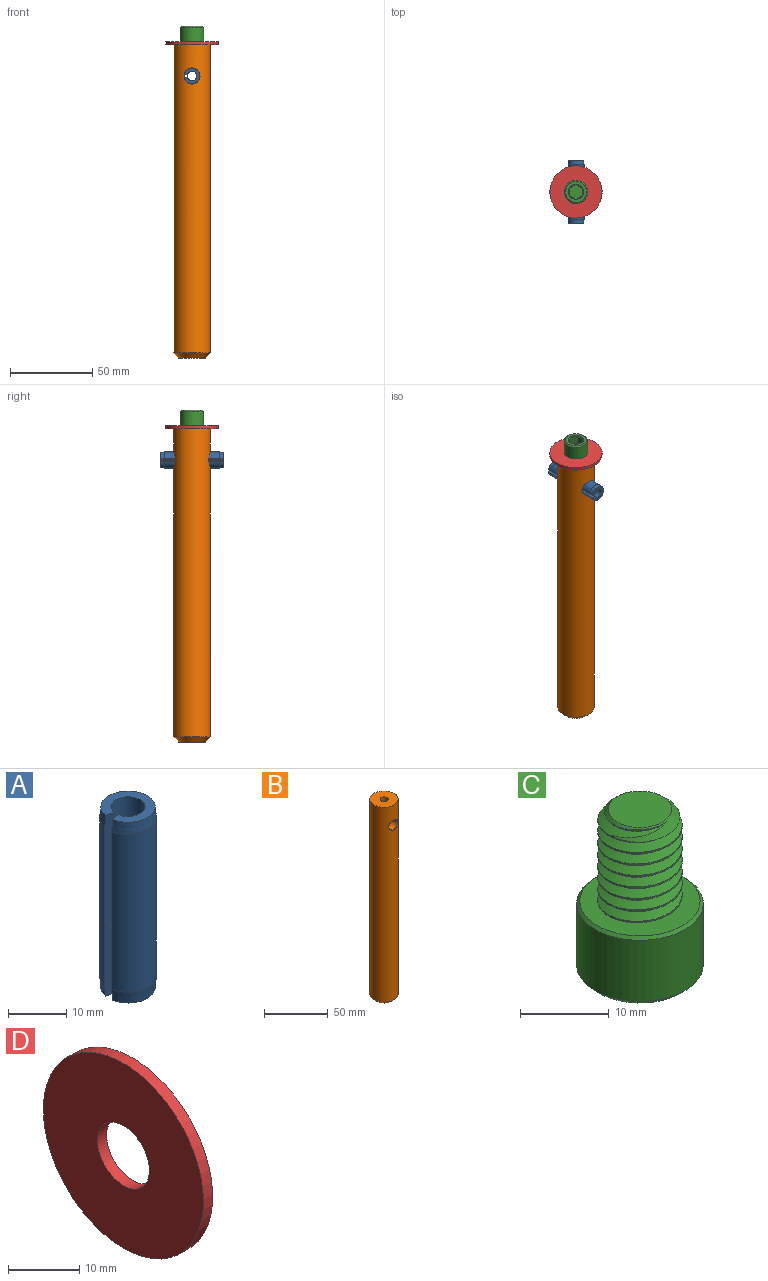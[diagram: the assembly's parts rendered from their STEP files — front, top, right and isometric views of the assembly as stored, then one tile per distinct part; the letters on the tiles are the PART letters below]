
ASSEMBLY  parts=4 mates=3
PART A: 8 faces, bbox 9.7x9.8x38.1 mm
  f0: cylinder r=2.93mm len=38.1mm, axis (0,0,-1), area 663.3mm2, adj f1,f3,f4,f5
  f1: plane 38.1x1.93mm, normal (-0.17,0.98,0), area 74mm2, adj f0,f2,f4,f5,f6,f7
  f2: cylinder r=4.89mm len=33.27mm, axis (0,0,-1), area 965.4mm2, adj f1,f3,f6,f7
  f3: plane 38.1x1.93mm, normal (-0.17,-0.98,0), area 74mm2, adj f0,f2,f4,f5,f6,f7
  f4: plane 9.35x9.28mm, normal (0,0,1), area 39.3mm2, adj f0,f1,f3,f7
  f5: plane 9.35x9.28mm, normal (0,0,-1), area 39.3mm2, adj f0,f1,f3,f6
  f6: cone r=4.89mm half-angle=5.1deg, axis (0,0,1), area 68.7mm2, adj f1,f2,f3,f5
  f7: cone r=4.67mm half-angle=5.1deg, axis (0,0,-1), area 68.7mm2, adj f1,f2,f3,f4
PART B: 7 faces, bbox 22.2x22.2x190.5 mm
  f0: cylinder r=11.11mm len=187.33mm, axis (0,0,-1), area 12933.5mm2, adj f1,f3,f4
  f1: plane 22.23x22.23mm, normal (0,0,1), area 356.3mm2, adj f0,f5
  f2: plane 15.88x15.88mm, normal (0,0,-1), area 197.9mm2, adj f3
  f3: cone r=11.11mm half-angle=45deg, axis (0,0,1), area 268.7mm2, adj f0,f2
  f4: cylinder r=4.76mm len=22.23mm, axis (0,-1,0), area 633.4mm2, adj f0
  f5: cylinder r=3.17mm len=12.7mm, axis (0,0,1), area 253.4mm2, adj f1,f6
  f6: plane 6.35x6.35mm, normal (0,0,1), area 31.7mm2, adj f5
PART C: 24 faces, bbox 16x16x24.6 mm
  f0: cylinder r=4.76mm len=11.51mm, axis (0,0,1), area 8mm2, adj f2,f4,f5,f6
  f1: plane 7.14x7.14mm, normal (0,0,1), area 40.1mm2, adj f2
  f2: cone r=3.57mm half-angle=45deg, axis (0,0,-1), area 24.1mm2, adj f0,f1,f3,f4,f5
  f3: cylinder r=3.73mm len=12.54mm, axis (0,0,-1), area 48.7mm2, adj f2,f4,f5,f6
  f4: bspline ~13.56x11mm, area 240.9mm2, adj f0,f2,f3,f6
  f5: bspline ~14.09x11mm, area 238.5mm2, adj f0,f2,f3,f6
  f6: plane 14.2x14.2mm, normal (0,0,1), area 87.6mm2, adj f0,f3,f4,f5,f23
  f7: cylinder r=7.14mm len=14.29mm, axis (0,0,1), area 379.4mm2, adj f22,f23
  f8: plane 12.86x12.86mm, normal (0,0,-1), area 63.9mm2, adj f9,f10,f11,f12,f13,f14,f22
  f9: cone r=4.58mm half-angle=45deg, axis (0,0,-1), area 0mm2, adj f8,f16
  f10: cone r=4.58mm half-angle=45deg, axis (0,0,-1), area 0mm2, adj f8,f17
  f11: cone r=4.58mm half-angle=45deg, axis (0,0,-1), area 0mm2, adj f8,f18
  f12: cone r=4.58mm half-angle=45deg, axis (0,0,-1), area 0mm2, adj f8,f19
  f13: cone r=4.58mm half-angle=45deg, axis (0,0,-1), area 0mm2, adj f8,f20
  f14: cone r=4.58mm half-angle=45deg, axis (0,0,-1), area 0mm2, adj f8,f21
  f15: plane 9.17x7.94mm, normal (0,0,-1), area 54.6mm2, adj f16,f17,f18,f19,f20,f21
  f16: plane 7.69x5.71mm, normal (-0.5,-0.87,0), area 25.4mm2, adj f9,f15,f17,f21
  f17: plane 7.69x6.33mm, normal (-1,0,0), area 25.4mm2, adj f10,f15,f16,f18
  f18: plane 7.69x5.71mm, normal (-0.5,0.87,0), area 25.4mm2, adj f11,f15,f17,f19
  f19: plane 7.69x5.71mm, normal (0.5,0.87,0), area 25.4mm2, adj f12,f15,f18,f20
  f20: plane 7.69x6.33mm, normal (1,0,0), area 25.4mm2, adj f13,f15,f19,f21
  f21: plane 7.69x5.71mm, normal (0.5,-0.87,0), area 25.4mm2, adj f14,f15,f16,f20
  f22: cone r=6.43mm half-angle=45deg, axis (0,0,1), area 43.1mm2, adj f7,f8
  f23: cone r=7.14mm half-angle=45deg, axis (0,0,-1), area 22.1mm2, adj f6,f7
PART D: 4 faces, bbox 1.8x31.8x31.8 mm
  f0: plane 31.75x31.75mm, normal (1,0,0), area 708.2mm2, adj f2,f3
  f1: plane 31.75x31.75mm, normal (-1,0,0), area 708.2mm2, adj f2,f3
  f2: cylinder r=15.88mm len=31.75mm, axis (-1,0,0), area 182.4mm2, adj f0,f1
  f3: cylinder r=5.16mm len=10.31mm, axis (-1,0,0), area 59.2mm2, adj f0,f1
PLACE A rot(axis=(-1,0,0),90deg) t=(-49.42,13.6,127.97)mm
PLACE B t=(-49.42,13.44,-43.48)mm
PLACE C rot(axis=(1,0,0),180deg) t=(-49.42,13.6,136.15)mm
PLACE D rot(axis=(0.71,0,-0.71),180deg) t=(-49.42,13.6,148.85)mm
MATE revolute A.f0 <-> B.f4  axis (0,-1,0) through (-49.42,13.6,127.97)mm
MATE fastened D.f2 <-> B.f0  axis (0,0,-1) through (-49.42,13.6,147.02)mm
MATE fastened C.f0 <-> D.f2  axis (0,0,-1) through (-49.42,13.6,148.85)mm
